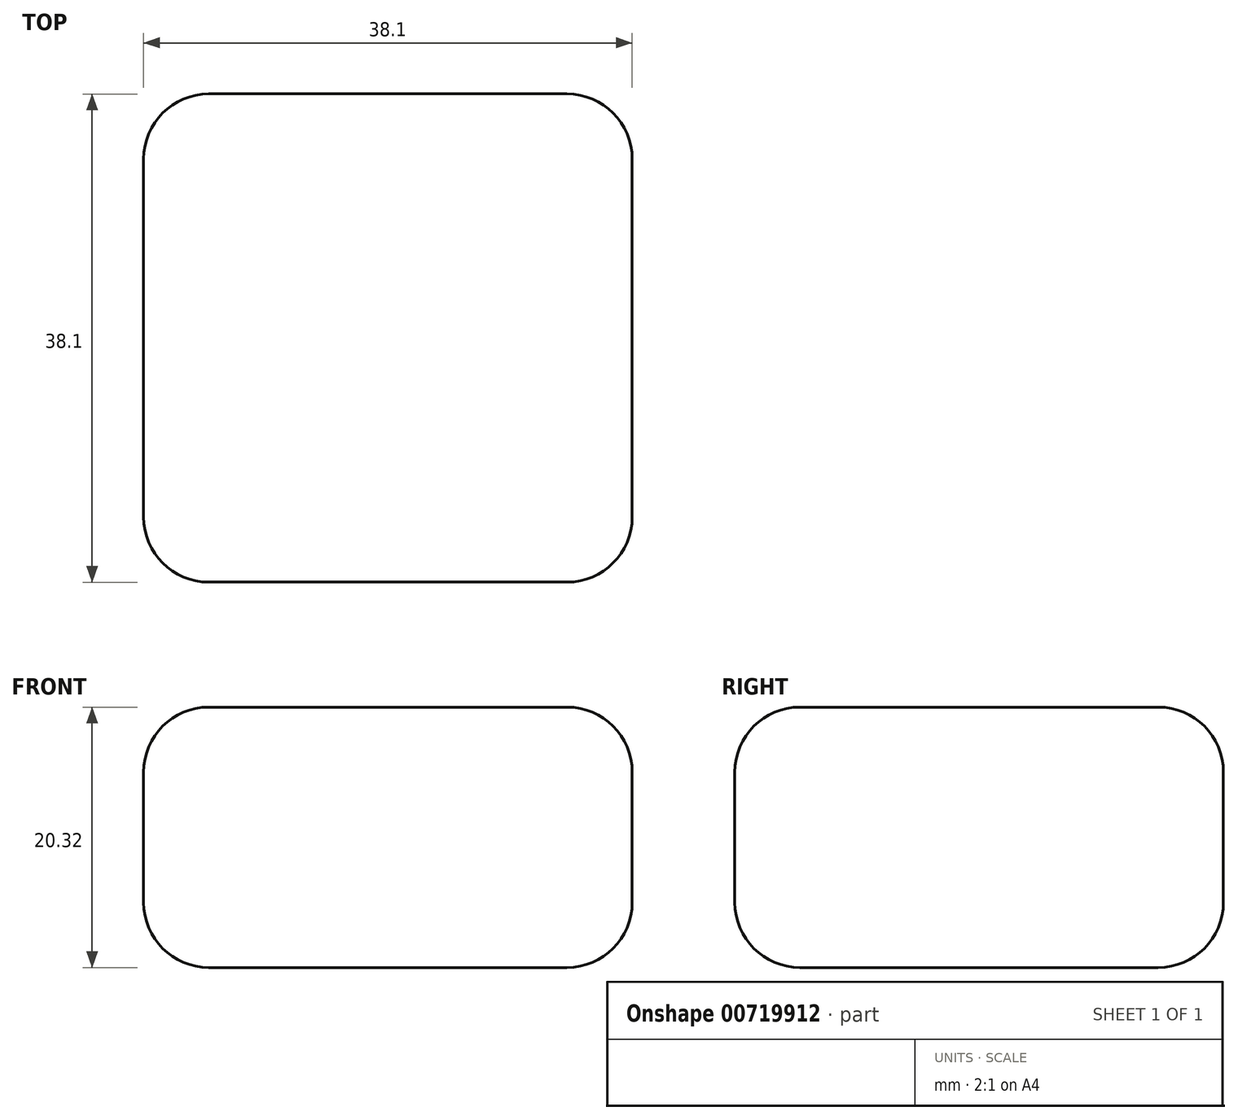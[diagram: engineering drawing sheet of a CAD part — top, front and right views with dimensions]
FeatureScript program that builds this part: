
annotation { "Feature Type Name" : "Feature", "Feature Type Description" : "" }
export const myFeature = defineFeature(function(context is Context, id is Id, definition is map)
    precondition{}
    {
        {
            var Q0;
            Q0=qCreatedBy(makeId("Top.planeOp"),FACE);
            var sketch = newSketch(context, id + "F0", { "sketchPlane" : qUnion([Q0])});
            skLineSegment(sketch, "E0.bottom", {"start": v(-62.39, -64.92) * mm, "end": v(-24.29, -64.92) * mm});
            skLineSegment(sketch, "E0.top", {"start": v(-62.39, -26.82) * mm, "end": v(-24.29, -26.82) * mm});
            skLineSegment(sketch, "E0.left", {"start": v(-62.39, -64.92) * mm, "end": v(-62.39, -26.82) * mm});
            skLineSegment(sketch, "E0.right", {"start": v(-24.29, -64.92) * mm, "end": v(-24.29, -26.82) * mm});
            skSolve(sketch);
        }
        {
            var Q0;
            Q0 = qSketchRegion(id + "F0", true);
            extrude(context, id + "F1", {"entities" : qUnion([Q0]), "depth" : 20.32 * mm, "offsetDistance" : 25.4 * mm});
        }
        {
            var Q0;
            Q0=makeQuery(id+"F1.opExtrude","CAP_FACE",FACE,{"disambiguationData":[OSD([sQuery(id+"F0.wireOp",EDGE,"E0.bottom"),sQuery(id+"F0.wireOp",EDGE,"E0.top"),sQuery(id+"F0.wireOp",EDGE,"E0.left"),sQuery(id+"F0.wireOp",EDGE,"E0.right")])],"isStart":false});
            var Q1;
            Q1=makeQuery(id+"F1.opExtrude","CAP_FACE",FACE,{"disambiguationData":[OSD([sQuery(id+"F0.wireOp",EDGE,"E0.bottom"),sQuery(id+"F0.wireOp",EDGE,"E0.top"),sQuery(id+"F0.wireOp",EDGE,"E0.left"),sQuery(id+"F0.wireOp",EDGE,"E0.right")])],"isStart":true});
            var Q2;
            Q2=makeQuery(id+"F1.opExtrude","SWEPT_FACE",FACE,{"disambiguationData":[OSD([sQuery(id+"F0.wireOp",EDGE,"E0.bottom")])]});
            var Q3;
            Q3=makeQuery(id+"F1.opExtrude","SWEPT_FACE",FACE,{"disambiguationData":[OSD([sQuery(id+"F0.wireOp",EDGE,"E0.top")])]});
            fillet(context, id + "F2", {"entities" : qUnion([Q0, Q1, Q2, Q3]), "radius" : 5.08 * mm, "tangentPropagation" : true, "allowEdgeOverflow" : false});
        }
    });
